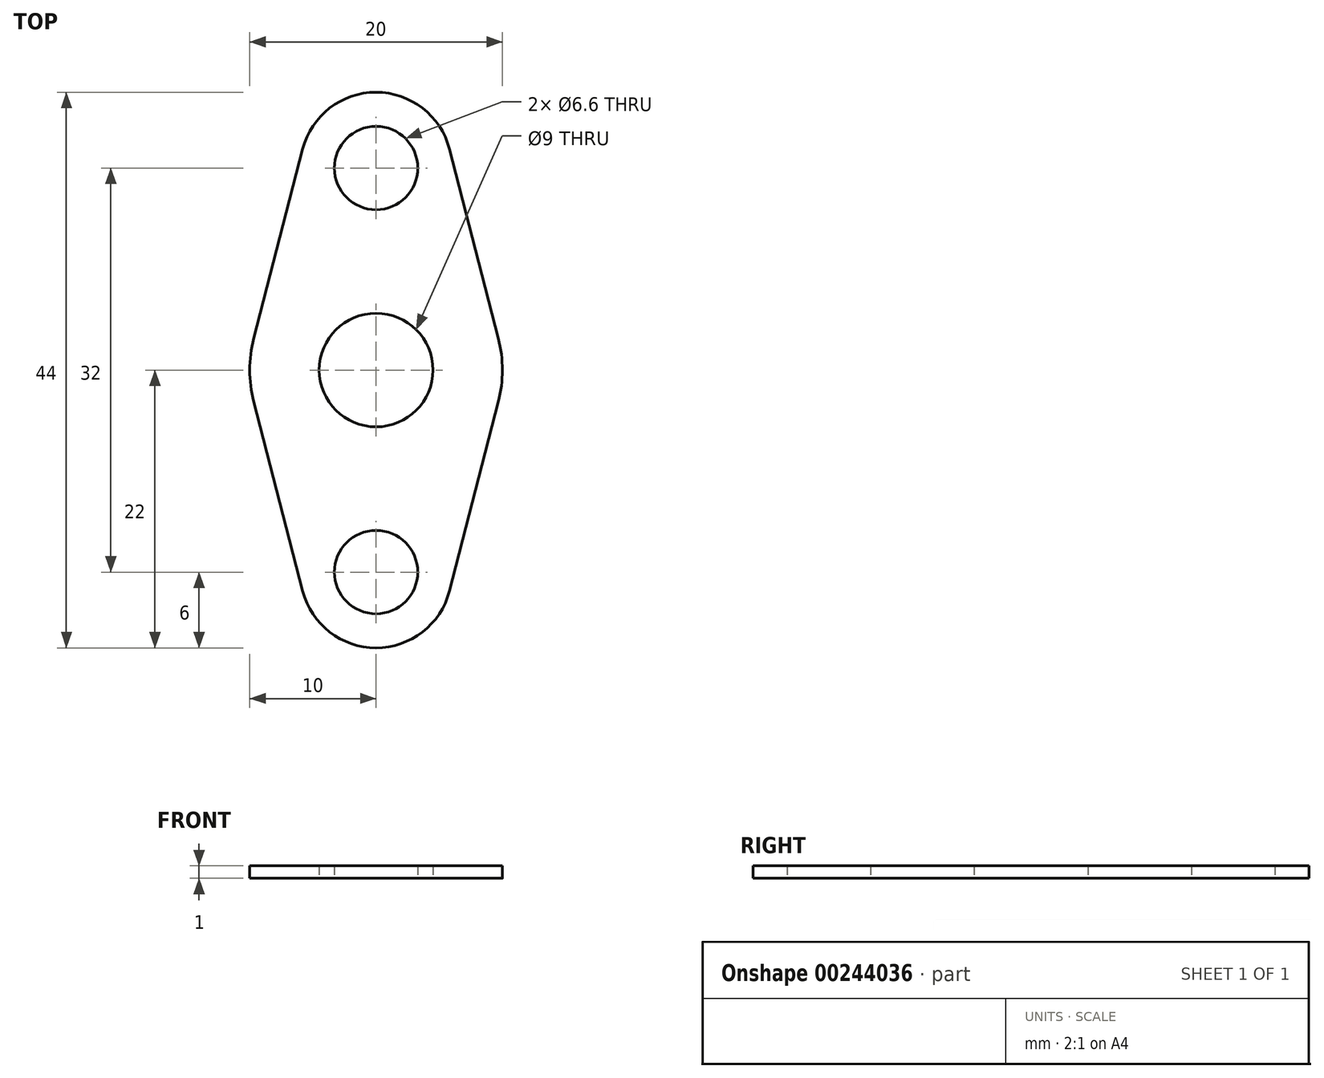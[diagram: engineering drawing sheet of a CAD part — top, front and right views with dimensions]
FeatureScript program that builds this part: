
annotation { "Feature Type Name" : "Feature", "Feature Type Description" : "" }
export const myFeature = defineFeature(function(context is Context, id is Id, definition is map)
    precondition{}
    {
        {
            var Q0;
            Q0=qCreatedBy(makeId("Top.planeOp"),FACE);
            var sketch = newSketch(context, id + "F0", { "sketchPlane" : qUnion([Q0])});
            skLineSegment(sketch, "E0", {"start": v(5.8, 17.5) * mm, "end": v(9.68, 2.5) * mm});
            skLineSegment(sketch, "E1", {"start": v(9.68, -2.5) * mm, "end": v(5.8, -17.5) * mm});
            skLineSegment(sketch, "E2.MirrorCS", {"start": v(-5.8, 17.5) * mm, "end": v(-9.68, 2.5) * mm});
            skLineSegment(sketch, "E3.MirrorCS", {"start": v(-9.68, -2.5) * mm, "end": v(-5.8, -17.5) * mm});
            skPoint(sketch, "E4.visualSharp", {"position": v(0, 40) * mm});
            skArc(sketch, "E4.filletArc", {"start": v(5.8, 17.5) * mm, "mid": v(0, 22) * mm, "end": v(-5.8, 17.5) * mm});
            skPoint(sketch, "E5.visualSharp", {"position": v(0, -40) * mm});
            skArc(sketch, "E5.filletArc", {"start": v(-5.8, -17.5) * mm, "mid": v(0, -22) * mm, "end": v(5.8, -17.5) * mm});
            skPoint(sketch, "E6.visualSharp", {"position": v(-10.33, 0) * mm});
            skArc(sketch, "E6.filletArc", {"start": v(-9.68, 2.5) * mm, "mid": v(-10, 0) * mm, "end": v(-9.68, -2.5) * mm});
            skPoint(sketch, "E7.visualSharp", {"position": v(10.33, 0) * mm});
            skArc(sketch, "E7.filletArc", {"start": v(9.68, -2.5) * mm, "mid": v(10, 0) * mm, "end": v(9.68, 2.5) * mm});
            skCircle(sketch, "E8", {"center": v(0, 0) * mm, "radius": 4.5 * mm});
            skCircle(sketch, "E9", {"center": v(0, 16) * mm, "radius": 3.3 * mm});
            skCircle(sketch, "E10", {"center": v(0, -16) * mm, "radius": 3.3 * mm});
            skSolve(sketch);
        }
        {
            var Q0;
            Q0=makeQuery(id+"F0.imprint","IMPRINT",FACE,{"disambiguationData":[TD([[makeQuery(id+"F0.imprint","IMPRINT",EDGE,{"derivedFrom":sQuery(id+"F0.wireOp",EDGE,"E0")}),-1.0]])]});
            extrude(context, id + "F1", {"entities" : qUnion([Q0]), "depth" : 1 * mm});
        }
    });
